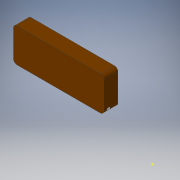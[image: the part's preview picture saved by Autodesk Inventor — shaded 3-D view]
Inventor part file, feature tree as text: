
AUTODESK INVENTOR PART (.ipt)
format: ipt  version: 2018 (Build 220112000, 112)  size: 383,488 bytes
history: native  units: in
note: dims shown in document units (in); Inventor stores cm internally (conversion verified against a paired STEP export)
features: other x4, extrude x1, boolean_combine x1, sketch x1, projected_geometry x1
ambient origin geometry x8: Origin, YZ Plane, XZ Plane, XY Plane, X Axis, Y Axis, Z Axis, Center Point
bodies: Solid1 (feature_tree), Solid2 (feature_tree)
feature tree (8):
  other  "drill back cavity to neck pickup cavity hole.iam"
  other  "Body.ipt:1"
  other  "Drill 12.ipt:1"
  extrude  "Extrusion1"  Depth=0.3937in TaperAngle=0.0deg
  boolean_combine  "Combine1"
  other  "Work Point1"
  sketch  "Sketch1"  dims[d0=0.3937in d1=1.0in d2=0.0in]
  projected_geometry  "Projected Loop1"
